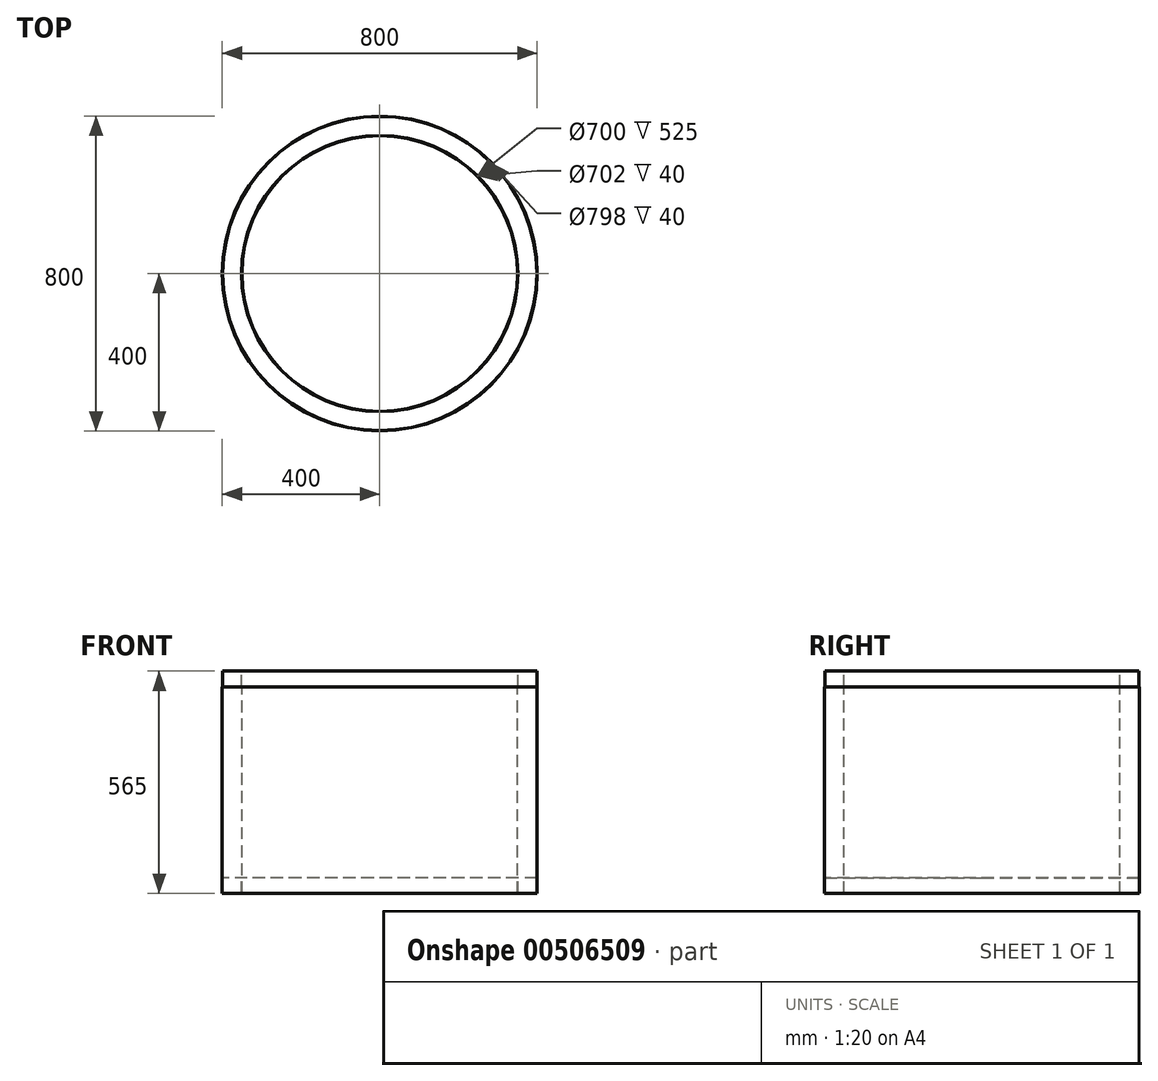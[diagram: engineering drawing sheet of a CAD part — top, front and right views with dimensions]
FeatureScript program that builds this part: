
annotation { "Feature Type Name" : "Feature", "Feature Type Description" : "" }
export const myFeature = defineFeature(function(context is Context, id is Id, definition is map)
    precondition{}
    {
        {
            var Q0;
            Q0=qCreatedBy(makeId("Front.planeOp"),FACE);
            var sketch = newSketch(context, id + "F0", { "sketchPlane" : qUnion([Q0])});
            skLineSegment(sketch, "E0", {"start": v(0, 74.87) * mm, "end": v(0, -73.71) * mm, "construction": true});
            skLineSegment(sketch, "E1", {"start": v(0, 374.84) * mm, "end": v(0, -528.94) * mm, "construction": true});
            skLineSegment(sketch, "E2", {"start": v(-350, -489.75) * mm, "end": v(-350, 35.25) * mm});
            skLineSegment(sketch, "E3", {"start": v(-350, 35.25) * mm, "end": v(-351, 35.25) * mm});
            skLineSegment(sketch, "E4", {"start": v(-351, 35.25) * mm, "end": v(-351, 75.25) * mm});
            skLineSegment(sketch, "E5", {"start": v(-351, 75.25) * mm, "end": v(-399, 75.25) * mm});
            skLineSegment(sketch, "E6", {"start": v(-399, 75.25) * mm, "end": v(-399, 35.25) * mm});
            skLineSegment(sketch, "E7", {"start": v(-399, 35.25) * mm, "end": v(-400, 35.25) * mm});
            skLineSegment(sketch, "E8", {"start": v(-400, 35.25) * mm, "end": v(-400, -489.75) * mm});
            skLineSegment(sketch, "E9", {"start": v(-400, -489.75) * mm, "end": v(-399, -489.75) * mm});
            skLineSegment(sketch, "E10", {"start": v(-399, -489.75) * mm, "end": v(-399, -449.75) * mm});
            skLineSegment(sketch, "E11", {"start": v(-399, -449.75) * mm, "end": v(-351, -449.75) * mm});
            skLineSegment(sketch, "E12", {"start": v(-351, -449.75) * mm, "end": v(-351, -489.75) * mm});
            skLineSegment(sketch, "E13", {"start": v(-351, -489.75) * mm, "end": v(-350, -489.75) * mm});
            skSolve(sketch);
        }
        {
            var Q0;
            Q0=qSketchRegion(id+"F0",true);
            var Q1;
            Q1=sQuery(id+"F0.wireOp",EDGE,"E1");
            revolve(context, id + "F1", {"entities" : qUnion([Q0]), "axis" : qUnion([Q1]), "revolveType" : RevolveType.FULL});
        }
    });
